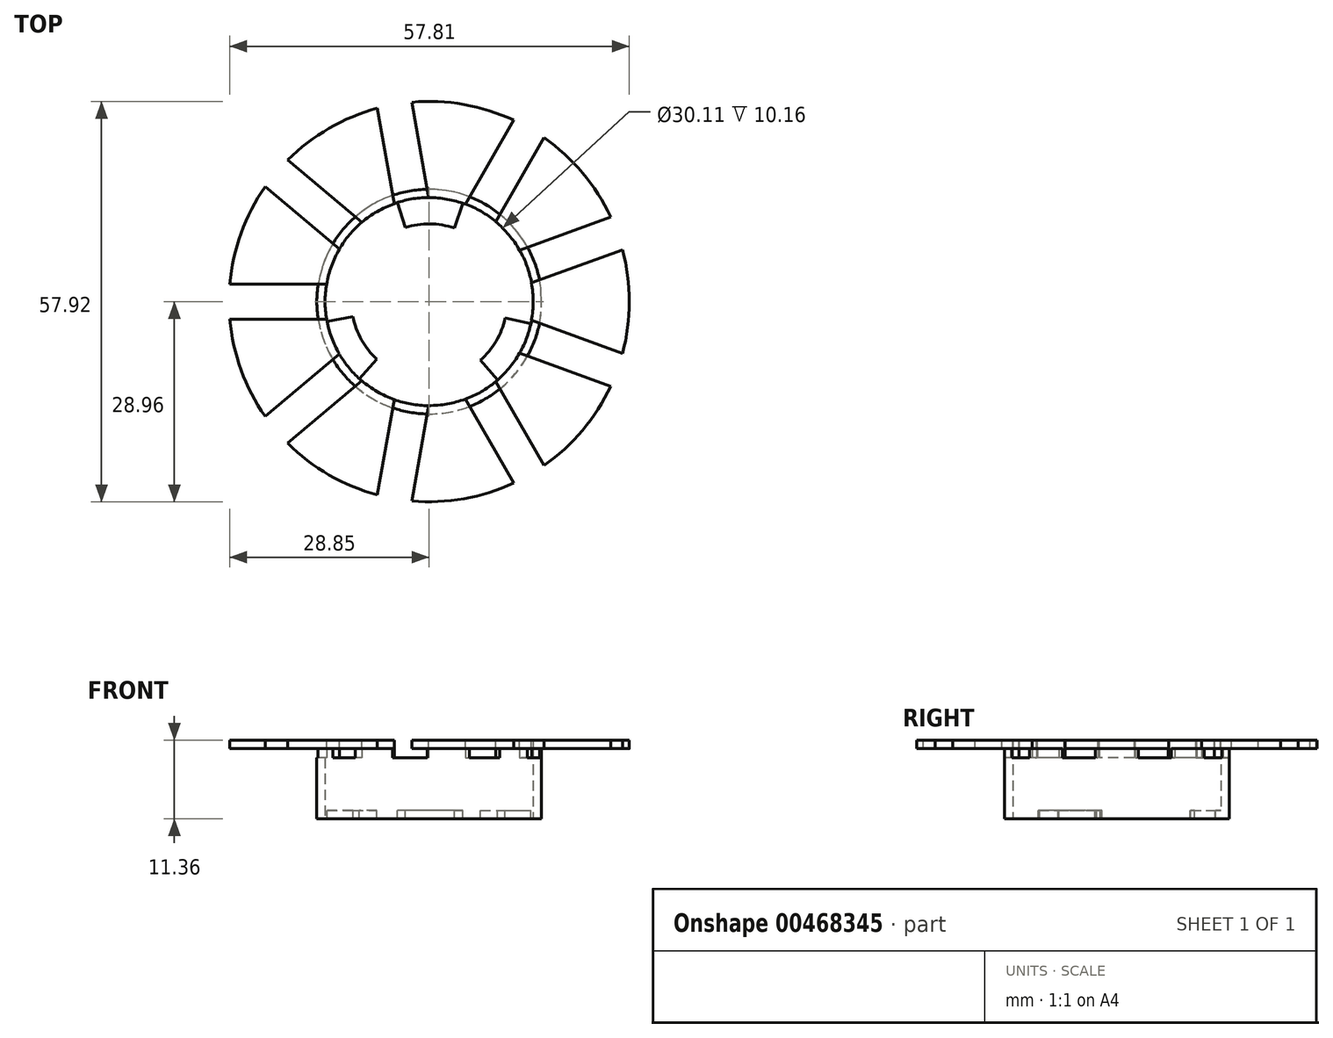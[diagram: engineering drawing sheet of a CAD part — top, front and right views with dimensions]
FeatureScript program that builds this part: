
annotation { "Feature Type Name" : "Feature", "Feature Type Description" : "" }
export const myFeature = defineFeature(function(context is Context, id is Id, definition is map)
    precondition{}
    {
        {
            var Q0;
            Q0=qCreatedBy(makeId("Top.planeOp"),FACE);
            var sketch = newSketch(context, id + "F0", { "sketchPlane" : qUnion([Q0])});
            skCircle(sketch, "E0", {"center": v(0, 0) * mm, "radius": 16.26 * mm});
            skSolve(sketch);
        }
        {
            var Q0;
            Q0 = qSketchRegion(id + "F0", true);
            extrude(context, id + "F1", {"entities" : qUnion([Q0]), "depth" : 10.16 * mm});
        }
        {
            var Q0;
            Q0=makeQuery(id+"F1.opExtrude","CAP_FACE",FACE,{"disambiguationData":[OSD([sQuery(id+"F0.wireOp",EDGE,"E0")])],"isStart":false});
            shell(context, id + "F2", {"entities" : qUnion([Q0]), "thickness" : 1.2 * mm});
        }
        {
            var Q0;
            Q0=makeQuery(id+"F1.opExtrude","CAP_FACE",FACE,{"disambiguationData":[OSD([sQuery(id+"F0.wireOp",EDGE,"E0")])],"isStart":false});
            var sketch = newSketch(context, id + "F3", { "sketchPlane" : qUnion([Q0])});
            skCircle(sketch, "E1", {"center": v(0, 0) * mm, "radius": 28.96 * mm});
            skCircle(sketch, "E2", {"center": v(0, 0) * mm, "radius": 15.04 * mm});
            skSolve(sketch);
        }
        {
            var Q0;
            Q0 = qSketchRegion(id + "F3", true);
            extrude(context, id + "F4", {"entities" : qUnion([Q0]), "operationType" : NewBodyOperationType.ADD, "depth" : 1.2 * mm});
        }
        {
            var Q0;
            Q0=makeQuery(id+"F4.opExtrude","CAP_FACE",FACE,{"disambiguationData":[OSD([sQuery(id+"F3.wireOp",EDGE,"E1"),sQuery(id+"F3.wireOp",EDGE,"E2")])],"isStart":false});
            var sketch = newSketch(context, id + "F5", { "sketchPlane" : qUnion([Q0])});
            skCircle(sketch, "E3", {"center": v(-15.04, 0) * mm, "radius": 2.54 * mm});
            skCircle(sketch, "E4.1.0", {"center": v(-11.52, -9.67) * mm, "radius": 2.54 * mm});
            skCircle(sketch, "E4.2.0", {"center": v(-2.61, -14.81) * mm, "radius": 2.54 * mm});
            skCircle(sketch, "E4.3.0", {"center": v(7.52, -13.02) * mm, "radius": 2.54 * mm});
            skCircle(sketch, "E4.4.0", {"center": v(14.13, -5.14) * mm, "radius": 2.54 * mm});
            skCircle(sketch, "E4.5.0", {"center": v(14.13, 5.14) * mm, "radius": 2.54 * mm});
            skCircle(sketch, "E4.6.0", {"center": v(7.52, 13.02) * mm, "radius": 2.54 * mm});
            skCircle(sketch, "E4.7.0", {"center": v(-2.61, 14.81) * mm, "radius": 2.54 * mm});
            skCircle(sketch, "E4.8.0", {"center": v(-11.52, 9.67) * mm, "radius": 2.54 * mm});
            skPoint(sketch, "E4.center", {"position": v(0, 0) * mm});
            skLineSegment(sketch, "E5", {"start": v(-14.83, 2.53) * mm, "end": v(-28.85, 2.53) * mm});
            skLineSegment(sketch, "E6", {"start": v(-14.83, -2.53) * mm, "end": v(-28.85, -2.53) * mm});
            skLineSegment(sketch, "E7.1.0", {"start": v(-12.98, -7.6) * mm, "end": v(-23.72, -16.6) * mm});
            skLineSegment(sketch, "E7.1.1", {"start": v(-9.73, -11.47) * mm, "end": v(-20.47, -20.48) * mm});
            skLineSegment(sketch, "E7.2.0", {"start": v(-5.07, -14.16) * mm, "end": v(-7.5, -27.97) * mm});
            skLineSegment(sketch, "E7.2.1", {"start": v(-0.08, -15.04) * mm, "end": v(-2.52, -28.85) * mm});
            skLineSegment(sketch, "E7.3.0", {"start": v(5.22, -14.1) * mm, "end": v(12.23, -26.25) * mm});
            skLineSegment(sketch, "E7.3.1", {"start": v(9.6, -11.57) * mm, "end": v(16.61, -23.72) * mm});
            skLineSegment(sketch, "E7.4.0", {"start": v(13.07, -7.45) * mm, "end": v(26.24, -12.24) * mm});
            skLineSegment(sketch, "E7.4.1", {"start": v(14.8, -2.7) * mm, "end": v(27.97, -7.49) * mm});
            skLineSegment(sketch, "E7.5.0", {"start": v(14.8, 2.7) * mm, "end": v(27.97, 7.49) * mm});
            skLineSegment(sketch, "E7.5.1", {"start": v(13.07, 7.45) * mm, "end": v(26.24, 12.24) * mm});
            skLineSegment(sketch, "E7.6.0", {"start": v(9.6, 11.57) * mm, "end": v(16.61, 23.72) * mm});
            skLineSegment(sketch, "E7.6.1", {"start": v(5.22, 14.1) * mm, "end": v(12.23, 26.25) * mm});
            skLineSegment(sketch, "E7.7.0", {"start": v(-0.08, 15.04) * mm, "end": v(-2.52, 28.85) * mm});
            skLineSegment(sketch, "E7.7.1", {"start": v(-5.07, 14.16) * mm, "end": v(-7.5, 27.97) * mm});
            skLineSegment(sketch, "E7.8.0", {"start": v(-9.73, 11.47) * mm, "end": v(-20.47, 20.48) * mm});
            skLineSegment(sketch, "E7.8.1", {"start": v(-12.98, 7.6) * mm, "end": v(-23.72, 16.6) * mm});
            skSolve(sketch);
        }
        {
            var Q0;
            {var subQ0=sQuery(id+"F5.wireOp",EDGE,"E7.8.0");var subQ1=sQuery(id+"F5.wireOp",EDGE,"E4.8.0");var subQ2=makeQuery(id+"F5.imprint","INTERSECT",VERTEX,{"derivedFrom":[subQ1,subQ0]});Q0=makeQuery(id+"F5.imprint","IMPRINT",FACE,{"disambiguationData":[TD([[makeQuery(id+"F5.imprint","IMPRINT",EDGE,{"disambiguationData":[TD([[subQ2,-1.0]])],"derivedFrom":subQ1}),-1.0]])]});}
            var Q1;
            {var subQ0=sQuery(id+"F5.wireOp",EDGE,"E7.7.0");var subQ1=sQuery(id+"F5.wireOp",EDGE,"E4.7.0");var subQ2=makeQuery(id+"F5.imprint","INTERSECT",VERTEX,{"derivedFrom":[subQ1,subQ0]});Q1=makeQuery(id+"F5.imprint","IMPRINT",FACE,{"disambiguationData":[TD([[makeQuery(id+"F5.imprint","IMPRINT",EDGE,{"disambiguationData":[TD([[subQ2,-1.0]])],"derivedFrom":subQ1}),-1.0]])]});}
            var Q2;
            {var subQ0=sQuery(id+"F5.wireOp",EDGE,"E7.6.0");var subQ1=sQuery(id+"F5.wireOp",EDGE,"E4.6.0");var subQ2=makeQuery(id+"F5.imprint","INTERSECT",VERTEX,{"derivedFrom":[subQ1,subQ0]});Q2=makeQuery(id+"F5.imprint","IMPRINT",FACE,{"disambiguationData":[TD([[makeQuery(id+"F5.imprint","IMPRINT",EDGE,{"disambiguationData":[TD([[subQ2,-1.0]])],"derivedFrom":subQ1}),-1.0]])]});}
            var Q3;
            {var subQ0=sQuery(id+"F5.wireOp",EDGE,"E7.5.0");var subQ1=sQuery(id+"F5.wireOp",EDGE,"E4.5.0");var subQ2=makeQuery(id+"F5.imprint","INTERSECT",VERTEX,{"derivedFrom":[subQ1,subQ0]});Q3=makeQuery(id+"F5.imprint","IMPRINT",FACE,{"disambiguationData":[TD([[makeQuery(id+"F5.imprint","IMPRINT",EDGE,{"disambiguationData":[TD([[subQ2,-1.0]])],"derivedFrom":subQ1}),-1.0]])]});}
            var Q4;
            {var subQ0=sQuery(id+"F5.wireOp",EDGE,"E7.4.0");var subQ1=sQuery(id+"F5.wireOp",EDGE,"E4.4.0");var subQ2=makeQuery(id+"F5.imprint","INTERSECT",VERTEX,{"derivedFrom":[subQ1,subQ0]});Q4=makeQuery(id+"F5.imprint","IMPRINT",FACE,{"disambiguationData":[TD([[makeQuery(id+"F5.imprint","IMPRINT",EDGE,{"disambiguationData":[TD([[subQ2,-1.0]])],"derivedFrom":subQ1}),-1.0]])]});}
            var Q5;
            {var subQ0=sQuery(id+"F5.wireOp",EDGE,"E7.3.0");var subQ1=sQuery(id+"F5.wireOp",EDGE,"E4.3.0");var subQ2=makeQuery(id+"F5.imprint","INTERSECT",VERTEX,{"derivedFrom":[subQ1,subQ0]});Q5=makeQuery(id+"F5.imprint","IMPRINT",FACE,{"disambiguationData":[TD([[makeQuery(id+"F5.imprint","IMPRINT",EDGE,{"disambiguationData":[TD([[subQ2,-1.0]])],"derivedFrom":subQ1}),-1.0]])]});}
            var Q6;
            {var subQ0=sQuery(id+"F5.wireOp",EDGE,"E7.2.0");var subQ1=sQuery(id+"F5.wireOp",EDGE,"E4.2.0");var subQ2=makeQuery(id+"F5.imprint","INTERSECT",VERTEX,{"derivedFrom":[subQ1,subQ0]});Q6=makeQuery(id+"F5.imprint","IMPRINT",FACE,{"disambiguationData":[TD([[makeQuery(id+"F5.imprint","IMPRINT",EDGE,{"disambiguationData":[TD([[subQ2,-1.0]])],"derivedFrom":subQ1}),-1.0]])]});}
            var Q7;
            {var subQ0=sQuery(id+"F5.wireOp",EDGE,"E7.1.0");var subQ1=sQuery(id+"F5.wireOp",EDGE,"E4.1.0");var subQ2=makeQuery(id+"F5.imprint","INTERSECT",VERTEX,{"derivedFrom":[subQ1,subQ0]});Q7=makeQuery(id+"F5.imprint","IMPRINT",FACE,{"disambiguationData":[TD([[makeQuery(id+"F5.imprint","IMPRINT",EDGE,{"disambiguationData":[TD([[subQ2,-1.0]])],"derivedFrom":subQ1}),-1.0]])]});}
            var Q8;
            {var subQ0=sQuery(id+"F5.wireOp",EDGE,"E5");var subQ1=sQuery(id+"F5.wireOp",EDGE,"E3");var subQ2=makeQuery(id+"F5.imprint","INTERSECT",VERTEX,{"derivedFrom":[subQ1,subQ0]});Q8=makeQuery(id+"F5.imprint","IMPRINT",FACE,{"disambiguationData":[TD([[makeQuery(id+"F5.imprint","IMPRINT",EDGE,{"disambiguationData":[TD([[subQ2,-1.0]])],"derivedFrom":subQ1}),-1.0]])]});}
            var Q9;
            {var subQ0=sQuery(id+"F5.wireOp",EDGE,"E5");var subQ1=sQuery(id+"F5.wireOp",EDGE,"E3");var subQ2=makeQuery(id+"F5.imprint","INTERSECT",VERTEX,{"derivedFrom":[subQ1,subQ0]});Q9=makeQuery(id+"F5.imprint","IMPRINT",FACE,{"disambiguationData":[TD([[makeQuery(id+"F5.imprint","IMPRINT",EDGE,{"disambiguationData":[TD([[subQ2,-1.0]])],"derivedFrom":subQ1}),1.0]])]});}
            var Q10;
            {var subQ0=sQuery(id+"F5.wireOp",EDGE,"E7.8.0");var subQ1=sQuery(id+"F5.wireOp",EDGE,"E4.8.0");var subQ2=makeQuery(id+"F5.imprint","INTERSECT",VERTEX,{"derivedFrom":[subQ1,subQ0]});Q10=makeQuery(id+"F5.imprint","IMPRINT",FACE,{"disambiguationData":[TD([[makeQuery(id+"F5.imprint","IMPRINT",EDGE,{"disambiguationData":[TD([[subQ2,-1.0]])],"derivedFrom":subQ1}),1.0]])]});}
            var Q11;
            {var subQ0=sQuery(id+"F5.wireOp",EDGE,"E7.7.0");var subQ1=sQuery(id+"F5.wireOp",EDGE,"E4.7.0");var subQ2=makeQuery(id+"F5.imprint","INTERSECT",VERTEX,{"derivedFrom":[subQ1,subQ0]});Q11=makeQuery(id+"F5.imprint","IMPRINT",FACE,{"disambiguationData":[TD([[makeQuery(id+"F5.imprint","IMPRINT",EDGE,{"disambiguationData":[TD([[subQ2,-1.0]])],"derivedFrom":subQ1}),1.0]])]});}
            var Q12;
            {var subQ0=sQuery(id+"F5.wireOp",EDGE,"E7.6.0");var subQ1=sQuery(id+"F5.wireOp",EDGE,"E4.6.0");var subQ2=makeQuery(id+"F5.imprint","INTERSECT",VERTEX,{"derivedFrom":[subQ1,subQ0]});Q12=makeQuery(id+"F5.imprint","IMPRINT",FACE,{"disambiguationData":[TD([[makeQuery(id+"F5.imprint","IMPRINT",EDGE,{"disambiguationData":[TD([[subQ2,-1.0]])],"derivedFrom":subQ1}),1.0]])]});}
            var Q13;
            {var subQ0=sQuery(id+"F5.wireOp",EDGE,"E7.5.0");var subQ1=sQuery(id+"F5.wireOp",EDGE,"E4.5.0");var subQ2=makeQuery(id+"F5.imprint","INTERSECT",VERTEX,{"derivedFrom":[subQ1,subQ0]});Q13=makeQuery(id+"F5.imprint","IMPRINT",FACE,{"disambiguationData":[TD([[makeQuery(id+"F5.imprint","IMPRINT",EDGE,{"disambiguationData":[TD([[subQ2,-1.0]])],"derivedFrom":subQ1}),1.0]])]});}
            var Q14;
            {var subQ0=sQuery(id+"F5.wireOp",EDGE,"E7.4.0");var subQ1=sQuery(id+"F5.wireOp",EDGE,"E4.4.0");var subQ2=makeQuery(id+"F5.imprint","INTERSECT",VERTEX,{"derivedFrom":[subQ1,subQ0]});Q14=makeQuery(id+"F5.imprint","IMPRINT",FACE,{"disambiguationData":[TD([[makeQuery(id+"F5.imprint","IMPRINT",EDGE,{"disambiguationData":[TD([[subQ2,-1.0]])],"derivedFrom":subQ1}),1.0]])]});}
            var Q15;
            {var subQ0=sQuery(id+"F5.wireOp",EDGE,"E7.3.0");var subQ1=sQuery(id+"F5.wireOp",EDGE,"E4.3.0");var subQ2=makeQuery(id+"F5.imprint","INTERSECT",VERTEX,{"derivedFrom":[subQ1,subQ0]});Q15=makeQuery(id+"F5.imprint","IMPRINT",FACE,{"disambiguationData":[TD([[makeQuery(id+"F5.imprint","IMPRINT",EDGE,{"disambiguationData":[TD([[subQ2,-1.0]])],"derivedFrom":subQ1}),1.0]])]});}
            var Q16;
            {var subQ0=sQuery(id+"F5.wireOp",EDGE,"E7.2.0");var subQ1=sQuery(id+"F5.wireOp",EDGE,"E4.2.0");var subQ2=makeQuery(id+"F5.imprint","INTERSECT",VERTEX,{"derivedFrom":[subQ1,subQ0]});Q16=makeQuery(id+"F5.imprint","IMPRINT",FACE,{"disambiguationData":[TD([[makeQuery(id+"F5.imprint","IMPRINT",EDGE,{"disambiguationData":[TD([[subQ2,-1.0]])],"derivedFrom":subQ1}),1.0]])]});}
            var Q17;
            {var subQ0=sQuery(id+"F5.wireOp",EDGE,"E7.1.0");var subQ1=sQuery(id+"F5.wireOp",EDGE,"E4.1.0");var subQ2=makeQuery(id+"F5.imprint","INTERSECT",VERTEX,{"derivedFrom":[subQ1,subQ0]});Q17=makeQuery(id+"F5.imprint","IMPRINT",FACE,{"disambiguationData":[TD([[makeQuery(id+"F5.imprint","IMPRINT",EDGE,{"disambiguationData":[TD([[subQ2,-1.0]])],"derivedFrom":subQ1}),1.0]])]});}
            extrude(context, id + "F6", {"entities" : qUnion([Q0, Q1, Q2, Q3, Q4, Q5, Q6, Q7, Q8, Q9, Q10, Q11, Q12, Q13, Q14, Q15, Q16, Q17]), "operationType" : NewBodyOperationType.REMOVE, "oppositeDirection" : true, "depth" : 2.54 * mm});
        }
        {
            var Q0;
            {var subQ0=sQuery(id+"F0.wireOp",EDGE,"E0");Q0=makeQuery(id+"F2.opShell","OFFSET_FACE",FACE,{"disambiguationData":[OSD([subQ0]),TDD([makeQuery(id+"F1.opExtrude","CAP_FACE",FACE,{"disambiguationData":[OSD([subQ0])],"isStart":true})])]});}
            var sketch = newSketch(context, id + "F7", { "sketchPlane" : qUnion([Q0])});
            skCircle(sketch, "E8", {"center": v(0, 0) * mm, "radius": 11.25 * mm});
            skLineSegment(sketch, "E9", {"start": v(3.65, 10.64) * mm, "end": v(4.89, 14.24) * mm});
            skLineSegment(sketch, "E10", {"start": v(-3.44, 10.7) * mm, "end": v(-4.6, 14.33) * mm});
            skCircle(sketch, "E11", {"center": v(0, 0) * mm, "radius": 15.06 * mm});
            skLineSegment(sketch, "E12.1.0", {"start": v(-7.55, -8.33) * mm, "end": v(-10.1, -11.16) * mm});
            skLineSegment(sketch, "E12.1.1", {"start": v(-11.04, -2.16) * mm, "end": v(-14.78, -2.89) * mm});
            skLineSegment(sketch, "E12.2.0", {"start": v(11, -2.37) * mm, "end": v(14.72, -3.18) * mm});
            skLineSegment(sketch, "E12.2.1", {"start": v(7.39, -8.48) * mm, "end": v(9.89, -11.35) * mm});
            skSolve(sketch);
        }
        {
            var Q0;
            {var subQ0=sQuery(id+"F7.wireOp",EDGE,"E12.1.0");Q0=makeQuery(id+"F7.imprint","IMPRINT",FACE,{"disambiguationData":[TD([[makeQuery(id+"F7.imprint","IMPRINT",EDGE,{"derivedFrom":subQ0}),1.0]])]});}
            var Q1;
            {var subQ0=sQuery(id+"F7.wireOp",EDGE,"E10");Q1=makeQuery(id+"F7.imprint","IMPRINT",FACE,{"disambiguationData":[TD([[makeQuery(id+"F7.imprint","IMPRINT",EDGE,{"derivedFrom":subQ0}),1.0]])]});}
            var Q2;
            {var subQ0=sQuery(id+"F7.wireOp",EDGE,"E9");Q2=makeQuery(id+"F7.imprint","IMPRINT",FACE,{"disambiguationData":[TD([[makeQuery(id+"F7.imprint","IMPRINT",EDGE,{"derivedFrom":subQ0}),-1.0]])]});}
            var Q3;
            {var subQ0=sQuery(id+"F7.wireOp",EDGE,"E8");var subQ5=makeQuery(id+"F7.imprint","INTERSECT",VERTEX,{"derivedFrom":[subQ0,sQuery(id+"F7.wireOp",EDGE,"E9")]});Q3=makeQuery(id+"F7.imprint","IMPRINT",FACE,{"disambiguationData":[TD([[makeQuery(id+"F7.imprint","IMPRINT",EDGE,{"disambiguationData":[TD([[subQ5,-1.0]])],"derivedFrom":subQ0}),1.0]])]});}
            extrude(context, id + "F8", {"entities" : qUnion([Q0, Q1, Q2, Q3]), "operationType" : NewBodyOperationType.REMOVE, "oppositeDirection" : true, "depth" : 25.4 * mm});
        }
    });
